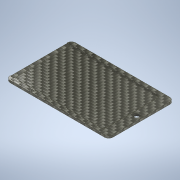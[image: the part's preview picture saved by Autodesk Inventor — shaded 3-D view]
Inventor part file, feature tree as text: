
AUTODESK INVENTOR PART (.ipt)
format: ipt  version: 2020 (Build 240168000, 168)  size: 162,816 bytes
history: native  units: in
note: dims shown in document units (in); Inventor stores cm internally (conversion verified against a paired STEP export)
features: extrude x4, fillet x2, sketch x1
ambient origin geometry x8: Origin, YZ Plane, XZ Plane, XY Plane, X Axis, Y Axis, Z Axis, Center Point
bodies: Solid1 (feature_tree)
feature tree (7):
  sketch  "Sketch1"  dims[d0=3.3701in d1=2.1252in d2=0.1252in d3=0.1252in d4=0.1575in d5=0.3543in d6=0.1969in d7=0.7874in d8=0.0787in d9=0.1181in d10=0.0787in d11=0.0in d12=0.0394in d13=0.0in d14=0.0787in d15=0.0in d16=0.0591in d17=0.0in d18=0.95in d19=0.1575in]
  extrude  "Extrusion1"  Depth=2.1252in
  extrude  "Extrusion2"  Depth=0.1252in
  extrude  "Extrusion3"  Depth=0.1252in
  extrude  "Extrusion4"  Depth=0.1575in
  fillet  "Fillet1"  Radius=0.3543in
  fillet  "Fillet2"  Radius=0.1969in
